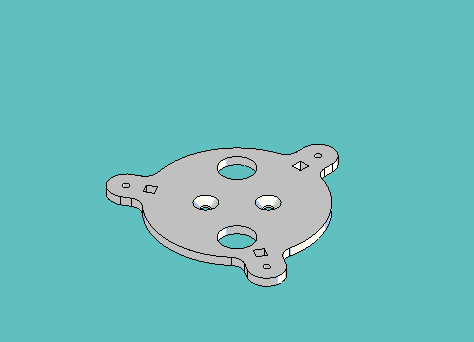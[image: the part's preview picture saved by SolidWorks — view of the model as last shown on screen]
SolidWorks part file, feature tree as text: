
SOLIDWORKS PART (.sldprt)
format: sldprt  version: not decoded by parser v0  size: 523,264 bytes
history: native  units: mm
features: sketch x4, extrude x2, pattern_circular x2, cut_extrude x2, chamfer x2, fillet x2, material x1 (+11 scaffold rows collapsed)
feature tree (26):
  scaffold x11  (default folders/planes/origin — collapsed)
  material  "Material <not specified>"
  sketch  "Sketch1"  dims[c1.D1=50.8mm c1.D7=3.175mm c2.D1=50.8mm c2.D2=~93.32036mm c3.D2=45.0deg c3.D3=~94.913632mm c4.D3=45.0deg c4.D4=6.35mm c4.D5=6.35mm c4.D6=31.75mm]
  extrude  "Extrude1"  Depth=3.175mm
  sketch  "Sketch2"  dims[c1.D1=50.8mm c1.D7=~3.96875mm c1.D2=~93.32036mm c2.D2=163.0deg c2.D3=~94.913632mm c3.D3=45.0deg c3.D4=4.7625mm c3.D5=4.7625mm c3.D6=31.75mm c3.D1=4.7625mm c4.D6=34.925mm]
  extrude  "Extrude2"  [1 undecoded]
  pattern_circular  "CirPattern1"  Count=2 Angle=86deg
  pattern_circular  "CirPattern2"  Count=2 Angle=223deg
  sketch  "Sketch3"  dims[D1=3.4544mm D2=3.4544mm]
  cut_extrude  "Cut-Extrude2"  [1 undecoded]
  chamfer  "Chamfer1"  Distance=2.38125mm Angle=45deg
  sketch  "Sketch5"  dims[c1.D3=19.05mm c1.D4=25.4mm c1.D1=20.6375mm c1.D2=20.6375mm c1.D5=~49.79749mm c2.D5=30.0deg c2.D6=11.1125mm c2.D1=17.145mm c2.D2=17.145mm c3.D1=~82.457251mm c4.D1=90.0deg c4.D2=9.525mm c4.D3=9.525mm]
  cut_extrude  "Cut-Extrude4"  [1 undecoded]
  fillet  "Fillet1"  Radius=4.7625mm
  chamfer  "Chamfer2"  Distance=1.5875mm Angle=45deg
  fillet  "Fillet2"  Radius=3.175mm
decode coverage: 11 of 14 modeling features carry decoded parameters
note: ~ marks probable driven/reference dimensions
note: 3 parameter values undecoded
summary: no parameter record found for 3 features
note: suppression state not decoded; provenance and decode notes live in map.json
